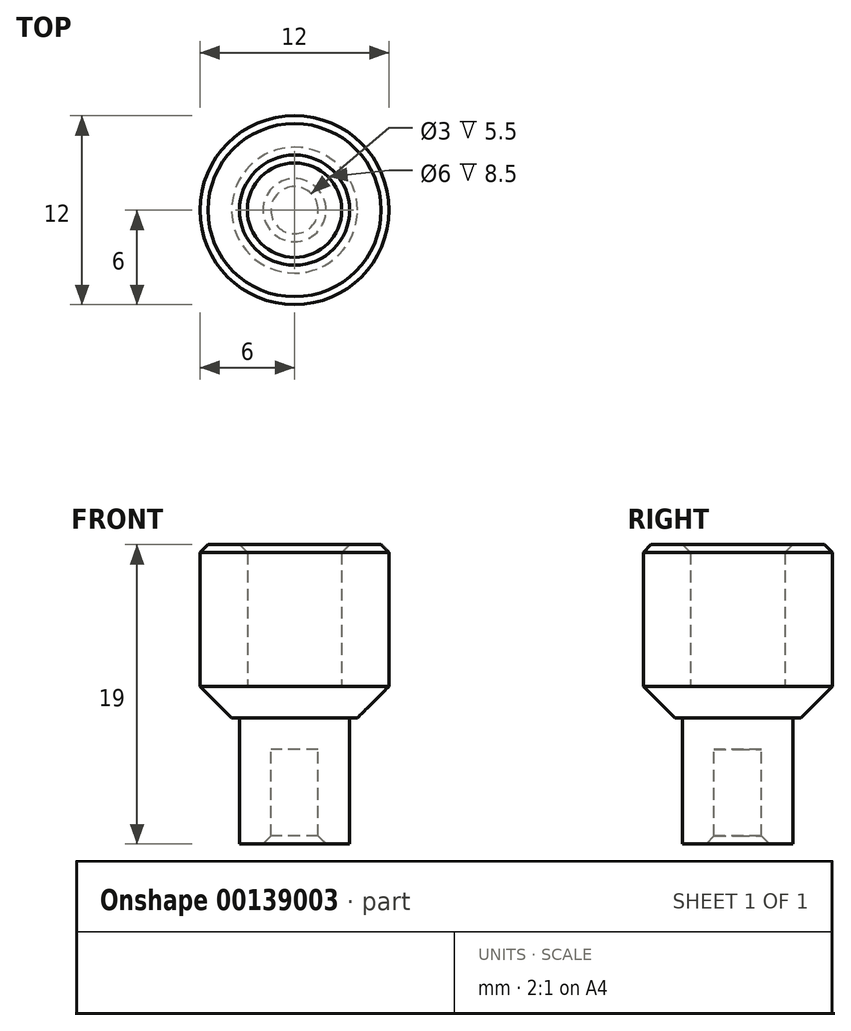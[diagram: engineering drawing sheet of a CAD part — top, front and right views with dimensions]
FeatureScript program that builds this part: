
annotation { "Feature Type Name" : "Feature", "Feature Type Description" : "" }
export const myFeature = defineFeature(function(context is Context, id is Id, definition is map)
    precondition{}
    {
        {
            var Q0;
            Q0=qCreatedBy(makeId("Top.planeOp"),FACE);
            var sketch = newSketch(context, id + "F0", { "sketchPlane" : qUnion([Q0])});
            skCircle(sketch, "E0", {"center": v(0, 0) * mm, "radius": 1.5 * mm});
            skCircle(sketch, "E1.0", {"center": v(0, 0) * mm, "radius": 3.5 * mm});
            skSolve(sketch);
        }
        {
            var Q0;
            Q0 = qSketchRegion(id + "F0", true);
            extrude(context, id + "F1", {"entities" : qUnion([Q0]), "oppositeDirection" : true, "depth" : 6 * mm});
        }
        {
            var Q0;
            Q0=makeQuery(id+"F1.opExtrude","CAP_FACE",FACE,{"disambiguationData":[OSD([sQuery(id+"F0.wireOp",EDGE,"E0"),sQuery(id+"F0.wireOp",EDGE,"E1.0")])],"isStart":true});
            var sketch = newSketch(context, id + "F2", { "sketchPlane" : qUnion([Q0])});
            skCircle(sketch, "E2.0", {"center": v(0, 0) * mm, "radius": 3.5 * mm});
            skCircle(sketch, "E3.1", {"center": v(0, 0) * mm, "radius": 1.5 * mm});
            skSolve(sketch);
        }
        {
            var Q0;
            Q0 = qSketchRegion(id + "F2", true);
            var Q1;
            Q1=makeQuery(id+"F2.imprint","IMPRINT",FACE,{"disambiguationData":[TD([[makeQuery(id+"F2.imprint","IMPRINT",EDGE,{"derivedFrom":sQuery(id+"F2.wireOp",EDGE,"E3.1")}),1.0]])]});
            extrude(context, id + "F3", {"entities" : qUnion([Q0, Q1]), "operationType" : NewBodyOperationType.ADD, "depth" : 2 * mm});
        }
        {
            var Q0;
            Q0=makeQuery(id+"F3.opExtrude","CAP_FACE",FACE,{"disambiguationData":[OSD([sQuery(id+"F2.wireOp",EDGE,"E2.0")])],"isStart":false});
            var sketch = newSketch(context, id + "F4", { "sketchPlane" : qUnion([Q0])});
            skCircle(sketch, "E4", {"center": v(0, 0) * mm, "radius": 3 * mm});
            skCircle(sketch, "E5.0", {"center": v(0, 0) * mm, "radius": 6 * mm});
            skSolve(sketch);
        }
        {
            var Q0;
            Q0=makeQuery(id+"F4.imprint","IMPRINT",FACE,{"disambiguationData":[TD([[makeQuery(id+"F4.imprint","IMPRINT",EDGE,{"derivedFrom":sQuery(id+"F4.wireOp",EDGE,"E4")}),-1.0]])]});
            var Q1;
            Q1=makeQuery(id+"F4.imprint","IMPRINT",FACE,{"disambiguationData":[TD([[makeQuery(id+"F4.imprint","IMPRINT",EDGE,{"derivedFrom":sQuery(id+"F4.wireOp",EDGE,"E4")}),1.0]])]});
            var Q2;
            Q2=makeQuery(id+"F4.imprint","IMPRINT",FACE,{"disambiguationData":[TD([[makeQuery(id+"F4.imprint","IMPRINT",EDGE,{"derivedFrom":makeQuery(id+"F3.opExtrude","CAP_EDGE",EDGE,{"disambiguationData":[OSD([sQuery(id+"F2.wireOp",EDGE,"E2.0")])],"isStart":false})}),1.0]])]});
            extrude(context, id + "F5", {"entities" : qUnion([Q0, Q1, Q2]), "operationType" : NewBodyOperationType.ADD, "depth" : 2 * mm});
        }
        {
            var Q0;
            Q0 = qSketchRegion(id + "F4", true);
            extrude(context, id + "F6", {"entities" : qUnion([Q0]), "operationType" : NewBodyOperationType.ADD, "depth" : 11 * mm});
        }
        {
            var Q0;
            Q0=makeQuery(id+"F6.opExtrude","CAP_EDGE",EDGE,{"disambiguationData":[OSD([sQuery(id+"F4.wireOp",EDGE,"E4")])],"isStart":false});
            var Q1;
            Q1=makeQuery(id+"F6.opExtrude","CAP_EDGE",EDGE,{"disambiguationData":[OSD([sQuery(id+"F4.wireOp",EDGE,"E5.0")])],"isStart":false});
            var Q2;
            Q2=makeQuery(id+"F1.opExtrude","CAP_EDGE",EDGE,{"disambiguationData":[OSD([sQuery(id+"F0.wireOp",EDGE,"E0")])],"isStart":false});
            chamfer(context, id + "F7", {"entities" : qUnion([Q0, Q1, Q2]), "width" : .5 * mm, "tangentPropagation" : true});
        }
        {
            var Q0;
            Q0=makeQuery(id+"F6.opExtrude","CAP_EDGE",EDGE,{"disambiguationData":[OSD([sQuery(id+"F4.wireOp",EDGE,"E5.0")])],"isStart":true});
            chamfer(context, id + "F8", {"entities" : qUnion([Q0]), "width" : 2 * mm, "tangentPropagation" : true});
        }
    });
